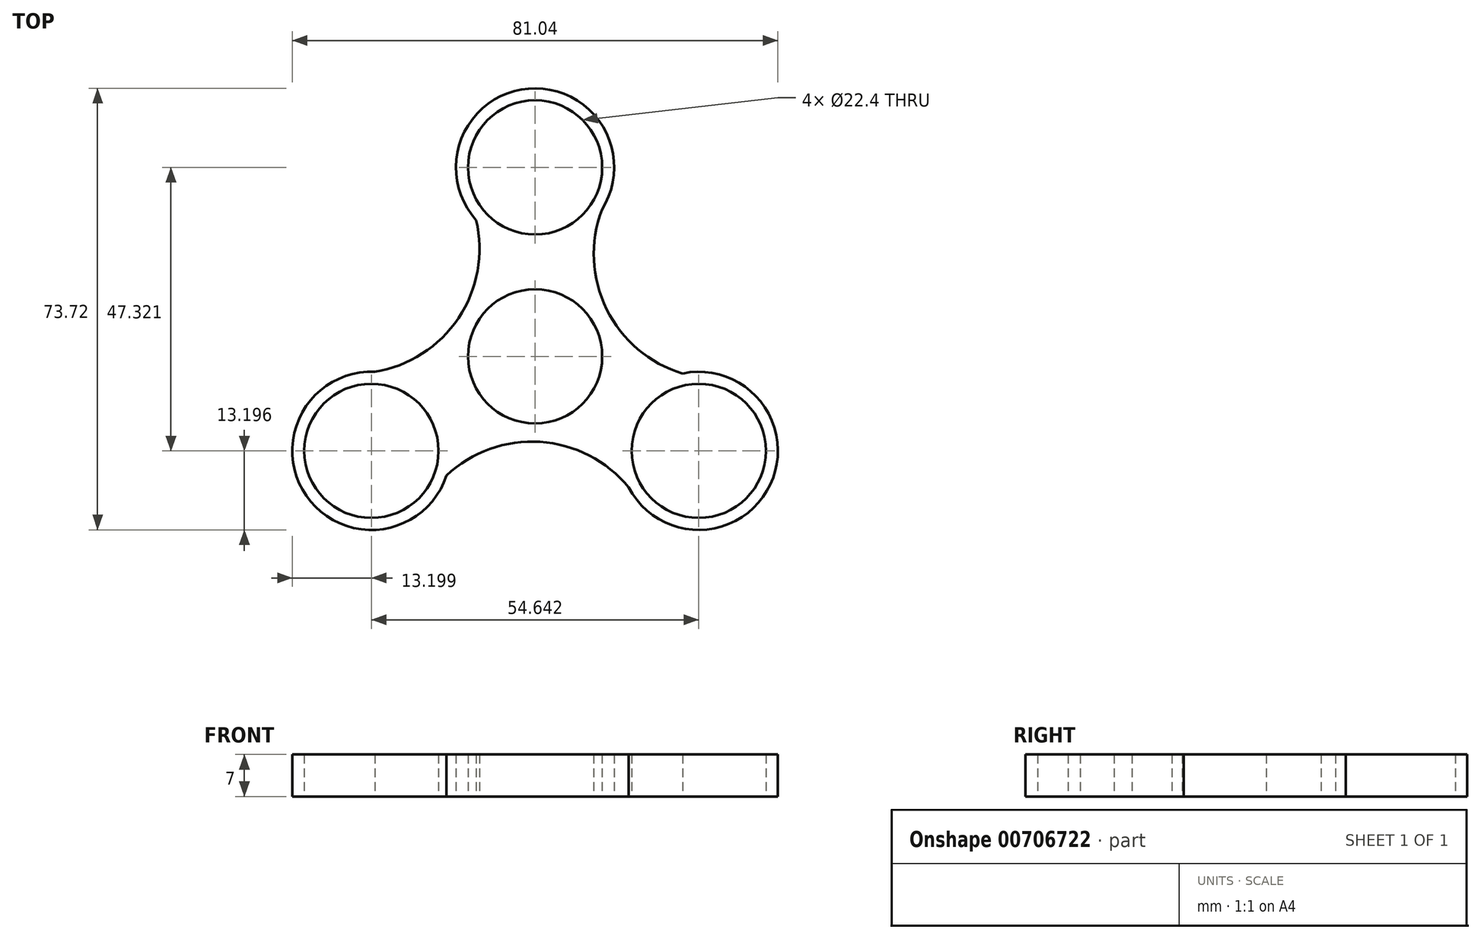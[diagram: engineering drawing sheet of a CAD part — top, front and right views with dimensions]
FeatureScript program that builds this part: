
annotation { "Feature Type Name" : "Feature", "Feature Type Description" : "" }
export const myFeature = defineFeature(function(context is Context, id is Id, definition is map)
    precondition{}
    {
        {
            var Q0;
            Q0=qCreatedBy(makeId("Top.planeOp"),FACE);
            var sketch = newSketch(context, id + "F0", { "sketchPlane" : qUnion([Q0])});
            skCircle(sketch, "E0", {"center": v(0, 0) * mm, "radius": 11.2 * mm});
            skCircle(sketch, "E1", {"center": v(0, 31.55) * mm, "radius": 11.2 * mm});
            skArc(sketch, "E2", {"start": v(11.14, 24.46) * mm, "mid": v(-1.08, 44.7) * mm, "end": v(-9.83, 22.74) * mm});
            skCircle(sketch, "E3.1.0", {"center": v(-27.32, -15.77) * mm, "radius": 11.2 * mm});
            skArc(sketch, "E3.1.1", {"start": v(-26.76, -2.59) * mm, "mid": v(-38.17, -23.29) * mm, "end": v(-14.78, -19.88) * mm});
            skCircle(sketch, "E3.2.0", {"center": v(27.32, -15.77) * mm, "radius": 11.2 * mm});
            skArc(sketch, "E3.2.1", {"start": v(15.62, -21.88) * mm, "mid": v(39.26, -21.41) * mm, "end": v(24.6, -2.86) * mm});
            skArc(sketch, "E4", {"start": v(12.55, 27.45) * mm, "mid": v(11.26, 9.39) * mm, "end": v(24.6, -2.86) * mm});
            skArc(sketch, "E5.1.0", {"start": v(-30.04, -2.86) * mm, "mid": v(-13.76, 5.06) * mm, "end": v(-9.83, 22.74) * mm});
            skArc(sketch, "E5.2.0", {"start": v(17.5, -24.59) * mm, "mid": v(2.5, -14.45) * mm, "end": v(-14.78, -19.88) * mm});
            skSolve(sketch);
        }
        {
            var Q0;
            Q0 = qSketchRegion(id + "F0", true);
            extrude(context, id + "F1", {"entities" : qUnion([Q0]), "depth" : 7 * mm, "offsetDistance" : 25 * mm});
        }
    });
